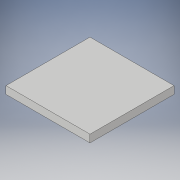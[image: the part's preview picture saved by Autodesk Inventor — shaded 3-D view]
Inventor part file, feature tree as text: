
AUTODESK INVENTOR PART (.ipt)
format: ipt  version: 2019 (Build 230136000, 136)  size: 91,648 bytes
history: native  units: mm
features: other x1, extrude x1, sketch x1
ambient origin geometry x8: Origin, YZ Plane, XZ Plane, XY Plane, X Axis, Y Axis, Z Axis, Center Point
bodies: Body1 (feature_tree)
feature tree (3):
  other  "Bryła1"
  extrude  "Wyciągnięcie proste1"  Depth=40.0mm
  sketch  "Szkic1"
